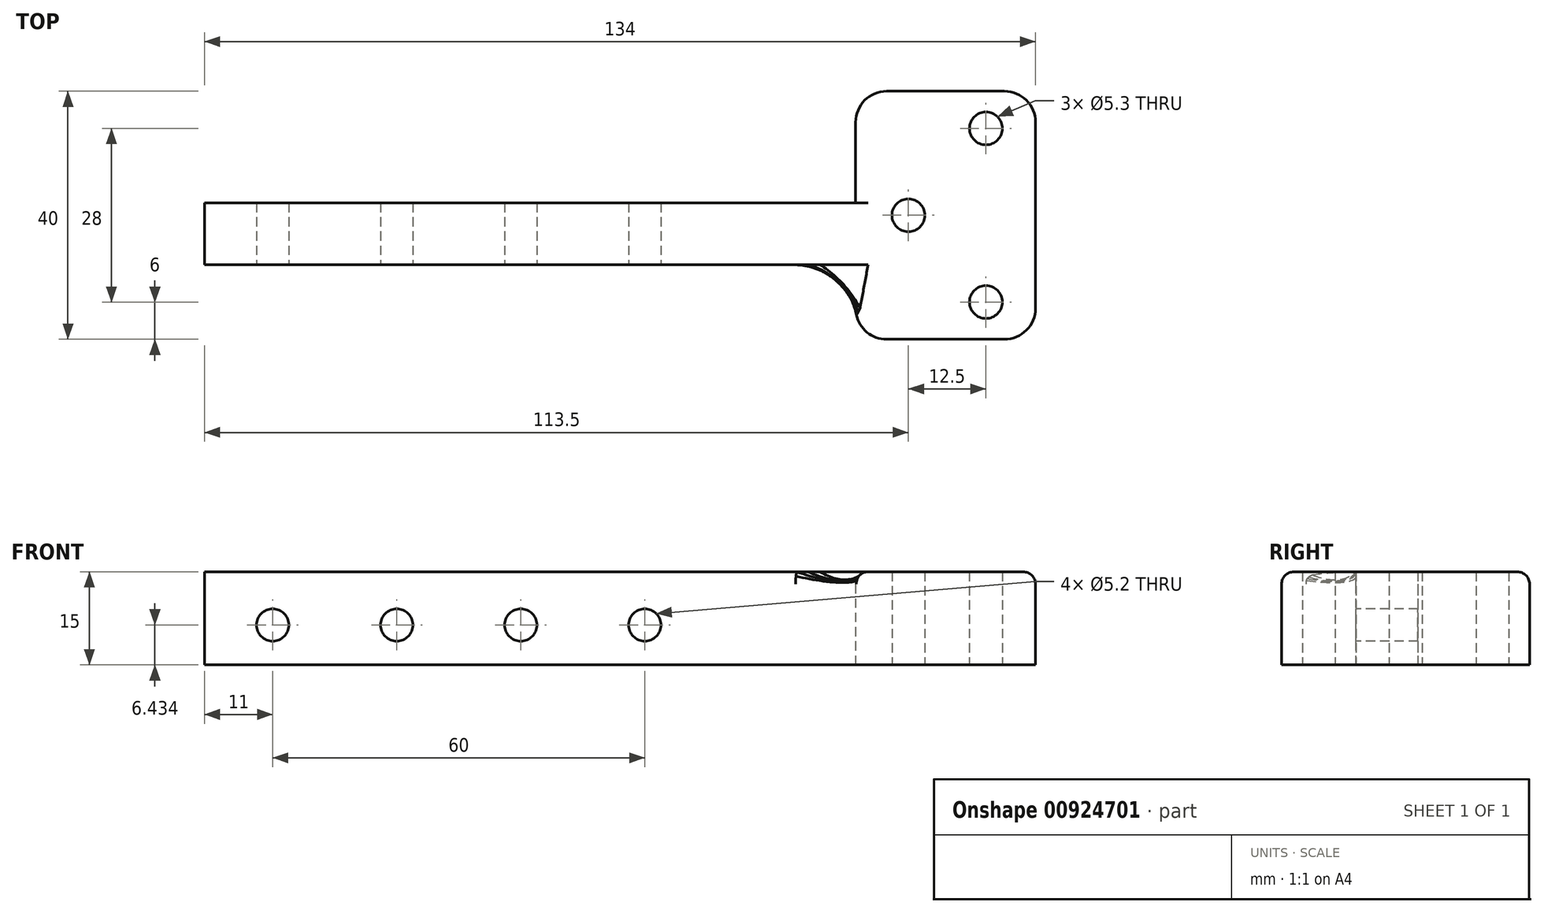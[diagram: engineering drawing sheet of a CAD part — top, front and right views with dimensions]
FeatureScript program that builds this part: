
annotation { "Feature Type Name" : "Feature", "Feature Type Description" : "" }
export const myFeature = defineFeature(function(context is Context, id is Id, definition is map)
    precondition{}
    {
        {
            var Q0;
            Q0=qCreatedBy(makeId("Top.planeOp"),FACE);
            var sketch = newSketch(context, id + "F0", { "sketchPlane" : qUnion([Q0])});
            skLineSegment(sketch, "E0.bottom", {"start": v(-8.5, 20) * mm, "end": v(20.5, 20) * mm});
            skLineSegment(sketch, "E0.top", {"start": v(-8.5, -20) * mm, "end": v(20.5, -20) * mm});
            skLineSegment(sketch, "E0.left", {"start": v(-8.5, 20) * mm, "end": v(-8.5, -20) * mm});
            skLineSegment(sketch, "E0.right", {"start": v(20.5, 20) * mm, "end": v(20.5, -20) * mm});
            skCircle(sketch, "E1", {"center": v(0, 0) * mm, "radius": 2.65 * mm});
            skCircle(sketch, "E2", {"center": v(12.5, 14) * mm, "radius": 2.65 * mm});
            skCircle(sketch, "E3", {"center": v(12.5, -14) * mm, "radius": 2.65 * mm});
            skLineSegment(sketch, "E4", {"start": v(0, -42.5) * mm, "end": v(0, 42.5) * mm, "construction": true});
            skLineSegment(sketch, "E5", {"start": v(0, -20) * mm, "end": v(0, -42.5) * mm, "construction": true});
            skLineSegment(sketch, "E6", {"start": v(0, 20) * mm, "end": v(0, 42.5) * mm, "construction": true});
            skLineSegment(sketch, "E7", {"start": v(-7.5, 20) * mm, "end": v(-7.5, -20) * mm, "construction": true});
            skLineSegment(sketch, "E8", {"start": v(-18.5, -20) * mm, "end": v(-18.5, -30) * mm, "construction": true});
            skLineSegment(sketch, "E9", {"start": v(-18.5, 20) * mm, "end": v(-18.5, 30) * mm, "construction": true});
            skLineSegment(sketch, "E10.bottom", {"start": v(-8.5, 2) * mm, "end": v(-113.5, 2) * mm});
            skLineSegment(sketch, "E10.top", {"start": v(-8.5, -8) * mm, "end": v(-113.5, -8) * mm});
            skLineSegment(sketch, "E10.left", {"start": v(-8.5, 2) * mm, "end": v(-8.5, -8) * mm});
            skLineSegment(sketch, "E10.right", {"start": v(-113.5, 2) * mm, "end": v(-113.5, -8) * mm});
            skSolve(sketch);
        }
        {
            var Q0;
            Q0=makeQuery(id+"F0.imprint","IMPRINT",FACE,{"disambiguationData":[TD([[makeQuery(id+"F0.imprint","IMPRINT",EDGE,{"derivedFrom":sQuery(id+"F0.wireOp",EDGE,"E0.bottom")}),-1.0]])]});
            var Q1;
            Q1=makeQuery(id+"F0.imprint","IMPRINT",FACE,{"disambiguationData":[TD([[makeQuery(id+"F0.imprint","IMPRINT",EDGE,{"derivedFrom":sQuery(id+"F0.wireOp",EDGE,"E10.bottom")}),1.0]])]});
            extrude(context, id + "F1", {"entities" : qUnion([Q0, Q1]), "depth" : 15 * mm, "offsetDistance" : 25 * mm});
        }
        {
            var Q0;
            Q0=makeQuery(id+"F1.opExtrude","SWEPT_EDGE",EDGE,{"disambiguationData":[OSD([sQuery(id+"F0.wireOp",EDGE,"E0.top"),sQuery(id+"F0.wireOp",EDGE,"E0.left")])]});
            var Q1;
            Q1=makeQuery(id+"F1.opExtrude","SWEPT_EDGE",EDGE,{"disambiguationData":[OSD([sQuery(id+"F0.wireOp",EDGE,"E0.top"),sQuery(id+"F0.wireOp",EDGE,"E0.right")])]});
            var Q2;
            Q2=makeQuery(id+"F1.opExtrude","SWEPT_EDGE",EDGE,{"disambiguationData":[OSD([sQuery(id+"F0.wireOp",EDGE,"E0.bottom"),sQuery(id+"F0.wireOp",EDGE,"E0.right")])]});
            var Q3;
            Q3=makeQuery(id+"F1.opExtrude","SWEPT_EDGE",EDGE,{"disambiguationData":[OSD([sQuery(id+"F0.wireOp",EDGE,"E0.bottom"),sQuery(id+"F0.wireOp",EDGE,"E0.left")])]});
            fillet(context, id + "F2", {"entities" : qUnion([Q0, Q1, Q2, Q3]), "radius" : 5 * mm, "tangentPropagation" : true, "allowEdgeOverflow" : false});
        }
        {
            var Q0;
            Q0=makeQuery(id+"F1.opExtrude","CAP_EDGE",EDGE,{"disambiguationData":[OSD([sQuery(id+"F0.wireOp",EDGE,"E0.bottom")])],"isStart":false});
            fillet(context, id + "F3", {"entities" : qUnion([Q0]), "radius" : 2 * mm, "tangentPropagation" : true, "allowEdgeOverflow" : false});
        }
        {
            var Q0;
            Q0=makeQuery(id+"F1.opExtrude","SWEPT_FACE",FACE,{"disambiguationData":[OSD([sQuery(id+"F0.wireOp",EDGE,"E10.top")])]});
            var sketch = newSketch(context, id + "F4", { "sketchPlane" : qUnion([Q0])});
            skCircle(sketch, "E11", {"center": v(-102.5, 6.43) * mm, "radius": 2.6 * mm});
            skCircle(sketch, "E12", {"center": v(-82.5, 6.43) * mm, "radius": 2.6 * mm});
            skCircle(sketch, "E13", {"center": v(-62.5, 6.43) * mm, "radius": 2.6 * mm});
            skCircle(sketch, "E14", {"center": v(-42.5, 6.43) * mm, "radius": 2.6 * mm});
            skSolve(sketch);
        }
        {
            var Q0;
            Q0 = qSketchRegion(id + "F4", true);
            extrude(context, id + "F5", {"entities" : qUnion([Q0]), "operationType" : NewBodyOperationType.REMOVE, "oppositeDirection" : true, "depth" : 25 * mm, "offsetDistance" : 25 * mm});
        }
        {
            var Q0;
            Q0=makeQuery(id+"F1.opExtrude","SWEPT_EDGE",EDGE,{"disambiguationData":[OSD([sQuery(id+"F0.wireOp",EDGE,"E0.left"),sQuery(id+"F0.wireOp",EDGE,"E10.top"),sQuery(id+"F0.wireOp",EDGE,"E10.left")])]});
            fillet(context, id + "F6", {"entities" : qUnion([Q0]), "radius" : 10 * mm, "tangentPropagation" : true, "allowEdgeOverflow" : false});
        }
    });
